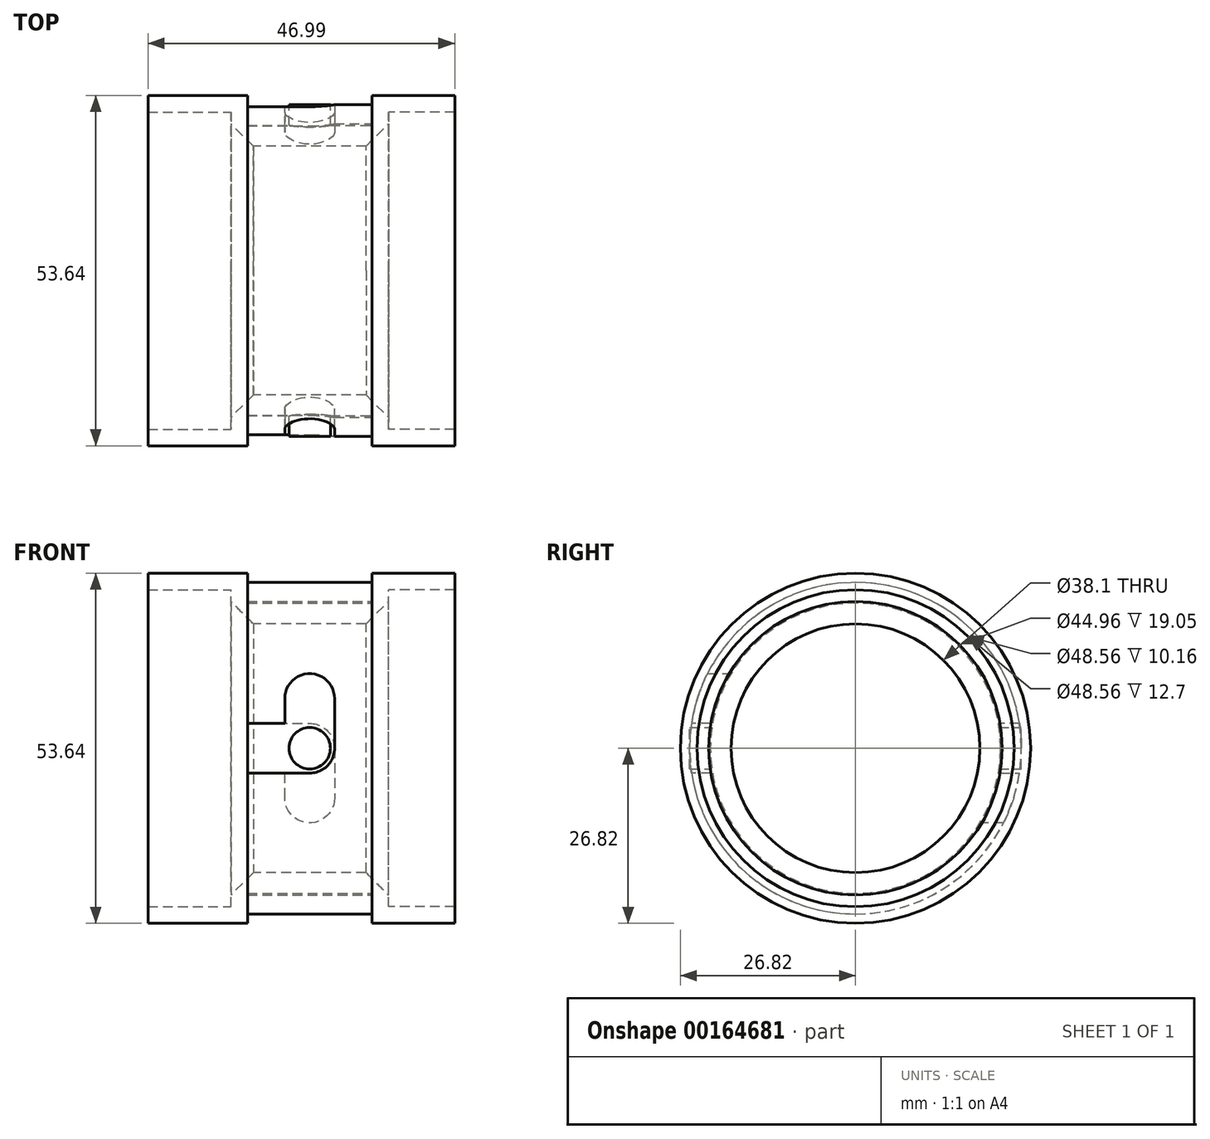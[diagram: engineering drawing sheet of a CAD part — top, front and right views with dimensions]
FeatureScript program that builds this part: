
annotation { "Feature Type Name" : "Feature", "Feature Type Description" : "" }
export const myFeature = defineFeature(function(context is Context, id is Id, definition is map)
    precondition{}
    {
        {
            var Q0;
            Q0=qCreatedBy(makeId("Right.planeOp"),FACE);
            var sketch = newSketch(context, id + "F0", { "sketchPlane" : qUnion([Q0])});
            skCircle(sketch, "E0", {"center": v(0, 0) * mm, "radius": 24.28 * mm});
            skCircle(sketch, "E1", {"center": v(0, 0) * mm, "radius": 26.82 * mm});
            skCircle(sketch, "E2", {"center": v(0, 0) * mm, "radius": 19.05 * mm});
            skSolve(sketch);
        }
        {
            var Q0;
            Q0=makeQuery(id+"F0.imprint","IMPRINT",FACE,{"disambiguationData":[TD([[makeQuery(id+"F0.imprint","IMPRINT",EDGE,{"derivedFrom":sQuery(id+"F0.wireOp",EDGE,"E0")}),-1.0]])]});
            var Q1;
            Q1=makeQuery(id+"F0.imprint","IMPRINT",FACE,{"disambiguationData":[TD([[makeQuery(id+"F0.imprint","IMPRINT",EDGE,{"derivedFrom":sQuery(id+"F0.wireOp",EDGE,"E0")}),1.0]])]});
            extrude(context, id + "F1", {"entities" : qUnion([Q0, Q1]), "depth" : 2.54 * mm});
        }
        {
            var Q0;
            Q0=makeQuery(id+"F0.imprint","IMPRINT",FACE,{"disambiguationData":[TD([[makeQuery(id+"F0.imprint","IMPRINT",EDGE,{"derivedFrom":sQuery(id+"F0.wireOp",EDGE,"E0")}),-1.0]])]});
            extrude(context, id + "F2", {"entities" : qUnion([Q0]), "operationType" : NewBodyOperationType.ADD, "depth" : 12.7 * mm});
        }
        {
            var Q0;
            Q0=qCreatedBy(makeId("Right.planeOp"),FACE);
            var sketch = newSketch(context, id + "F3", { "sketchPlane" : qUnion([Q0])});
            skCircle(sketch, "E3", {"center": v(0, 0) * mm, "radius": 22.48 * mm});
            skCircle(sketch, "E4", {"center": v(0, 0) * mm, "radius": 25.4 * mm});
            skSolve(sketch);
        }
        {
            var Q0;
            Q0=qSketchRegion(id+"F3",true);
            extrude(context, id + "F4", {"entities" : qUnion([Q0]), "operationType" : NewBodyOperationType.ADD, "oppositeDirection" : true, "depth" : 19.05 * mm});
        }
        {
            var Q0;
            Q0=qCreatedBy(makeId("Front.planeOp"),FACE);
            var sketch = newSketch(context, id + "F5", { "sketchPlane" : qUnion([Q0])});
            skLineSegment(sketch, "E5", {"start": v(0, 0) * mm, "end": v(-19.05, 0) * mm, "construction": true});
            skLineSegment(sketch, "E6", {"start": v(-19.05, -3.81) * mm, "end": v(-19.05, 3.8) * mm});
            skLineSegment(sketch, "E7", {"start": v(-19.05, 3.8) * mm, "end": v(-9.53, 3.8) * mm});
            skLineSegment(sketch, "E8", {"start": v(-9.53, 3.8) * mm, "end": v(-9.52, -3.8) * mm});
            skLineSegment(sketch, "E9", {"start": v(-9.52, -3.81) * mm, "end": v(-19.05, -3.81) * mm});
            skSolve(sketch);
        }
        {
            var Q0;
            Q0=qSketchRegion(id+"F5",true);
            extrude(context, id + "F6", {"entities" : qUnion([Q0]), "operationType" : NewBodyOperationType.REMOVE, "oppositeDirection" : true, "depth" : 50.8 * mm, "hasSecondDirection" : true, "secondDirectionOppositeDirection" : false, "secondDirectionDepth" : 50.8 * mm});
        }
        {
            var Q0;
            Q0=qCreatedBy(makeId("Front.planeOp"),FACE);
            var sketch = newSketch(context, id + "F7", { "sketchPlane" : qUnion([Q0])});
            skLineSegment(sketch, "E10", {"start": v(0, 0) * mm, "end": v(-9.53, 0) * mm, "construction": true});
            skCircle(sketch, "E11", {"center": v(-9.53, 0) * mm, "radius": 3.81 * mm});
            skSolve(sketch);
        }
        {
            var Q0;
            Q0=qSketchRegion(id+"F7",true);
            extrude(context, id + "F8", {"entities" : qUnion([Q0]), "operationType" : NewBodyOperationType.REMOVE, "oppositeDirection" : true, "depth" : 50.8 * mm, "hasSecondDirection" : true, "secondDirectionOppositeDirection" : false, "secondDirectionDepth" : 50.8 * mm});
        }
        {
            var Q0;
            Q0=qCreatedBy(makeId("Front.planeOp"),FACE);
            var sketch = newSketch(context, id + "F9", { "sketchPlane" : qUnion([Q0])});
            skLineSegment(sketch, "E12", {"start": v(0, 0) * mm, "end": v(-9.53, 0) * mm, "construction": true});
            skLineSegment(sketch, "E13", {"start": v(-9.53, 0) * mm, "end": v(-9.53, 7.62) * mm, "construction": true});
            skCircle(sketch, "E14", {"center": v(-9.53, 7.62) * mm, "radius": 3.81 * mm});
            skLineSegment(sketch, "E15", {"start": v(-9.53, 7.62) * mm, "end": v(-13.34, 7.62) * mm, "construction": true});
            skLineSegment(sketch, "E16", {"start": v(-13.34, 7.62) * mm, "end": v(-13.34, 0) * mm});
            skLineSegment(sketch, "E17", {"start": v(-13.34, 0) * mm, "end": v(-5.72, 0) * mm});
            skLineSegment(sketch, "E18", {"start": v(-5.72, 0) * mm, "end": v(-5.72, 7.62) * mm});
            skSolve(sketch);
        }
        {
            var Q0;
            {var subQ0=sQuery(id+"F9.wireOp",EDGE,"E14");var subQ1=makeQuery(id+"F9.imprint","INTERSECT",VERTEX,{"derivedFrom":[subQ0,sQuery(id+"F9.wireOp",EDGE,"E16")]});Q0=makeQuery(id+"F9.imprint","IMPRINT",FACE,{"disambiguationData":[TD([[makeQuery(id+"F9.imprint","IMPRINT",EDGE,{"disambiguationData":[TD([[subQ1,1.0]])],"derivedFrom":subQ0}),1.0]])]});}
            var Q1;
            {var subQ0=sQuery(id+"F9.wireOp",EDGE,"E16");Q1=makeQuery(id+"F9.imprint","IMPRINT",FACE,{"disambiguationData":[TD([[makeQuery(id+"F9.imprint","IMPRINT",EDGE,{"derivedFrom":subQ0}),1.0]])]});}
            var Q2;
            Q2=sQuery(id+"F9.wireOp",EDGE,"E15");
            extrude(context, id + "F10", {"entities" : qUnion([Q0, Q1]), "operationType" : NewBodyOperationType.REMOVE, "surfaceEntities" : qUnion([Q2]), "depth" : 50.8 * mm});
        }
        {
            var Q0;
            Q0=qCreatedBy(makeId("Front.planeOp"),FACE);
            var sketch = newSketch(context, id + "F11", { "sketchPlane" : qUnion([Q0])});
            skLineSegment(sketch, "E19", {"start": v(0, 0) * mm, "end": v(-9.53, 0) * mm, "construction": true});
            skLineSegment(sketch, "E20", {"start": v(-9.53, 0) * mm, "end": v(-9.53, -7.62) * mm, "construction": true});
            skCircle(sketch, "E21", {"center": v(-9.53, -7.62) * mm, "radius": 3.81 * mm});
            skLineSegment(sketch, "E22", {"start": v(-9.53, -7.62) * mm, "end": v(-13.33, -7.62) * mm, "construction": true});
            skLineSegment(sketch, "E23", {"start": v(-13.33, -7.62) * mm, "end": v(-13.33, 0) * mm});
            skLineSegment(sketch, "E24", {"start": v(-13.33, 0) * mm, "end": v(-5.72, 0) * mm});
            skLineSegment(sketch, "E25", {"start": v(-5.71, 0) * mm, "end": v(-5.71, -7.62) * mm});
            skSolve(sketch);
        }
        {
            var Q0;
            {var subQ0=sQuery(id+"F11.wireOp",EDGE,"E23");Q0=makeQuery(id+"F11.imprint","IMPRINT",FACE,{"disambiguationData":[TD([[makeQuery(id+"F11.imprint","IMPRINT",EDGE,{"derivedFrom":subQ0}),-1.0]])]});}
            var Q1;
            {var subQ0=sQuery(id+"F11.wireOp",EDGE,"E21");var subQ1=makeQuery(id+"F11.imprint","INTERSECT",VERTEX,{"derivedFrom":[subQ0,sQuery(id+"F11.wireOp",EDGE,"E23")]});Q1=makeQuery(id+"F11.imprint","IMPRINT",FACE,{"disambiguationData":[TD([[makeQuery(id+"F11.imprint","IMPRINT",EDGE,{"disambiguationData":[TD([[subQ1,1.0]])],"derivedFrom":subQ0}),1.0]])]});}
            var Q2;
            Q2=sQuery(id+"F11.wireOp",EDGE,"E22");
            extrude(context, id + "F12", {"entities" : qUnion([Q0, Q1]), "operationType" : NewBodyOperationType.REMOVE, "surfaceEntities" : qUnion([Q2]), "oppositeDirection" : true, "depth" : 25.4 * mm});
        }
        {
            var Q0;
            Q0=qCreatedBy(makeId("Right.planeOp"),FACE);
            var sketch = newSketch(context, id + "F13", { "sketchPlane" : qUnion([Q0])});
            skCircle(sketch, "E26", {"center": v(0, 0) * mm, "radius": 19.05 * mm});
            skCircle(sketch, "E27", {"center": v(0, 0) * mm, "radius": 22.23 * mm});
            skCircle(sketch, "E28", {"center": v(0, 0) * mm, "radius": 24.28 * mm});
            skSolve(sketch);
        }
        {
            var Q0;
            Q0=makeQuery(id+"F13.imprint","IMPRINT",FACE,{"disambiguationData":[TD([[makeQuery(id+"F13.imprint","IMPRINT",EDGE,{"derivedFrom":sQuery(id+"F13.wireOp",EDGE,"E26")}),-1.0]])]});
            extrude(context, id + "F14", {"entities" : qUnion([Q0]), "oppositeDirection" : true, "depth" : 21.59 * mm});
        }
        {
            var Q0;
            Q0=makeQuery(id+"F13.imprint","IMPRINT",FACE,{"disambiguationData":[TD([[makeQuery(id+"F13.imprint","IMPRINT",EDGE,{"derivedFrom":sQuery(id+"F13.wireOp",EDGE,"E27")}),-1.0]])]});
            extrude(context, id + "F15", {"entities" : qUnion([Q0]), "operationType" : NewBodyOperationType.ADD, "oppositeDirection" : true, "depth" : 21.59 * mm, "hasSecondDirection" : true, "secondDirectionOppositeDirection" : true, "secondDirectionDepth" : 19.05 * mm});
        }
        {
            var Q0;
            Q0=qCreatedBy(makeId("Right.planeOp"),FACE);
            var sketch = newSketch(context, id + "F16", { "sketchPlane" : qUnion([Q0])});
            skCircle(sketch, "E29", {"center": v(0, 0) * mm, "radius": 24.28 * mm});
            skCircle(sketch, "E30", {"center": v(0, 0) * mm, "radius": 26.82 * mm});
            skSolve(sketch);
        }
        {
            var Q0;
            Q0=qSketchRegion(id+"F16",true);
            extrude(context, id + "F17", {"entities" : qUnion([Q0]), "operationType" : NewBodyOperationType.ADD, "oppositeDirection" : true, "depth" : 34.3 * mm, "hasSecondDirection" : true, "secondDirectionOppositeDirection" : true, "secondDirectionDepth" : 19.05 * mm});
        }
        {
            var Q0;
            Q0=qCreatedBy(makeId("Front.planeOp"),FACE);
            var sketch = newSketch(context, id + "F18", { "sketchPlane" : qUnion([Q0])});
            skLineSegment(sketch, "E31", {"start": v(0, 0) * mm, "end": v(-9.52, 0) * mm, "construction": true});
            skCircle(sketch, "E32", {"center": v(-9.52, 0) * mm, "radius": 3.18 * mm});
            skSolve(sketch);
        }
        {
            var Q0;
            Q0=qSketchRegion(id+"F18",true);
            extrude(context, id + "F19", {"entities" : qUnion([Q0]), "operationType" : NewBodyOperationType.ADD, "depth" : 25.4 * mm, "hasSecondDirection" : true, "secondDirectionOppositeDirection" : true, "secondDirectionDepth" : 25.4 * mm});
        }
        {
            var Q0;
            Q0=makeQuery(id+"F13.imprint","IMPRINT",FACE,{"disambiguationData":[TD([[makeQuery(id+"F13.imprint","IMPRINT",EDGE,{"derivedFrom":sQuery(id+"F13.wireOp",EDGE,"E26")}),1.0]])]});
            extrude(context, id + "F20", {"entities" : qUnion([Q0]), "operationType" : NewBodyOperationType.REMOVE, "oppositeDirection" : true, "depth" : 25.4 * mm});
        }
        {
            var Q0;
            Q0=qCreatedBy(makeId("Front.planeOp"),FACE);
            var sketch = newSketch(context, id + "F21", { "sketchPlane" : qUnion([Q0])});
            skLineSegment(sketch, "E33", {"start": v(0, 0) * mm, "end": v(24.47, 0) * mm, "construction": true});
            skLineSegment(sketch, "E34", {"start": v(0, 0) * mm, "end": v(0, -22.48) * mm, "construction": true});
            skLineSegment(sketch, "E35", {"start": v(0, 0) * mm, "end": v(0, -19.94) * mm, "construction": true});
            skLineSegment(sketch, "E36", {"start": v(0, -22.48) * mm, "end": v(2.54, -22.48) * mm, "construction": true});
            skLineSegment(sketch, "E37", {"start": v(2.54, -22.48) * mm, "end": v(2.54, -19.94) * mm});
            skLineSegment(sketch, "E38", {"start": v(2.54, -19.94) * mm, "end": v(0, -19.94) * mm});
            skLineSegment(sketch, "E39", {"start": v(0, -19.94) * mm, "end": v(2.54, -22.48) * mm});
            skLineSegment(sketch, "E40", {"start": v(0, -19.94) * mm, "end": v(0, -19.05) * mm});
            skLineSegment(sketch, "E41", {"start": v(0, -19.05) * mm, "end": v(2.54, -19.05) * mm});
            skLineSegment(sketch, "E42", {"start": v(2.54, -19.05) * mm, "end": v(2.54, -19.94) * mm});
            skLineSegment(sketch, "E43", {"start": v(0, -19.94) * mm, "end": v(-0.89, -19.05) * mm});
            skLineSegment(sketch, "E44", {"start": v(-0.89, -19.05) * mm, "end": v(0, -19.05) * mm});
            skLineSegment(sketch, "E45", {"start": v(0, -19.05) * mm, "end": v(0, -19.94) * mm});
            skSolve(sketch);
        }
        {
            var Q0;
            Q0=qSketchRegion(id+"F21",true);
            var Q1;
            Q1=sQuery(id+"F21.wireOp",EDGE,"E33");
            revolve(context, id + "F22", {"operationType" : NewBodyOperationType.REMOVE, "entities" : qUnion([Q0]), "axis" : qUnion([Q1]), "revolveType" : RevolveType.FULL, "oppositeDirection" : true});
        }
        {
            var Q0;
            Q0=qCreatedBy(makeId("Front.planeOp"),FACE);
            var sketch = newSketch(context, id + "F23", { "sketchPlane" : qUnion([Q0])});
            skLineSegment(sketch, "E46", {"start": v(0, 0) * mm, "end": v(-21.59, 0) * mm, "construction": true});
            skLineSegment(sketch, "E47", {"start": v(-21.59, 0) * mm, "end": v(-21.59, -19.05) * mm, "construction": true});
            skLineSegment(sketch, "E48", {"start": v(-21.59, -19.05) * mm, "end": v(-21.59, -22.48) * mm});
            skLineSegment(sketch, "E49", {"start": v(-21.59, -22.48) * mm, "end": v(-18.16, -19.05) * mm});
            skLineSegment(sketch, "E50", {"start": v(-18.16, -19.05) * mm, "end": v(-21.59, -19.05) * mm});
            skSolve(sketch);
        }
        {
            var Q0;
            Q0=makeQuery(id+"F23.imprint","IMPRINT",FACE,{"disambiguationData":[TD([[makeQuery(id+"F23.imprint","IMPRINT",EDGE,{"derivedFrom":sQuery(id+"F23.wireOp",EDGE,"E48")}),1.0]])]});
            var Q1;
            Q1=sQuery(id+"F23.wireOp",EDGE,"E46");
            revolve(context, id + "F24", {"operationType" : NewBodyOperationType.REMOVE, "entities" : qUnion([Q0]), "axis" : qUnion([Q1]), "revolveType" : RevolveType.FULL, "oppositeDirection" : true});
        }
        {
            var Q0;
            Q0=qSketchRegion(id+"F21",true);
            var Q1;
            Q1=sQuery(id+"F21.wireOp",EDGE,"E33");
            revolve(context, id + "F25", {"operationType" : NewBodyOperationType.REMOVE, "entities" : qUnion([Q0]), "axis" : qUnion([Q1]), "revolveType" : RevolveType.FULL, "oppositeDirection" : true});
        }
    });
